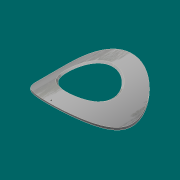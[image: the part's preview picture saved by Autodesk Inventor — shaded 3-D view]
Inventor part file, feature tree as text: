
AUTODESK INVENTOR PART (.ipt)
format: ipt  version: 2017.3 (Build 213257000, 257)  size: 195,072 bytes
history: native  units: in
note: dims shown in document units (in); Inventor stores cm internally (conversion verified against a paired STEP export)
features: sketch x5, extrude x2, sweep x1, plane x1, hole x1
ambient origin geometry x8: Origin, YZ Plane, XZ Plane, XY Plane, X Axis, Y Axis, Z Axis, Center Point
bodies: Solid1 (feature_tree)
feature tree (10):
  extrude  "Extrusion1"  Depth=35.0in
  extrude  "Extrusion2"  Depth=14.001in
  sketch  "Sketch3"  dims[d5=26.001in d6=26.0in d7=0.0in]
  sweep  "Sweep1"
  plane  "Work Plane1"
  hole  "Hole1"  [1 undecoded]
  sketch  "Sketch1"  dims[d0=34.0in d1=35.0in]
  sketch  "Sketch2"  dims[d2=26.001in d3=0.0in d4=14.001in]
  sketch  "3D Sketch1"
  sketch  "Sketch4"  dims[d9=0.25in d10=0.25in d11=0.2749in d12=0.5in d13=0.0in d14=0.0in d15=0.0625in d16=0.2979in d17=12.0005in d18=0.422in d19=0.395in d20=0.0246in d21=0.423in d22=0.375in d23=0.25in d24=0.5635in d25=1.0in d26=0.8108in]
note: 1 required parameter value undecoded (feature->parameter linkage not recoverable at this tier; creation-order binding heuristic only, values carry confidence <= 0.55)
